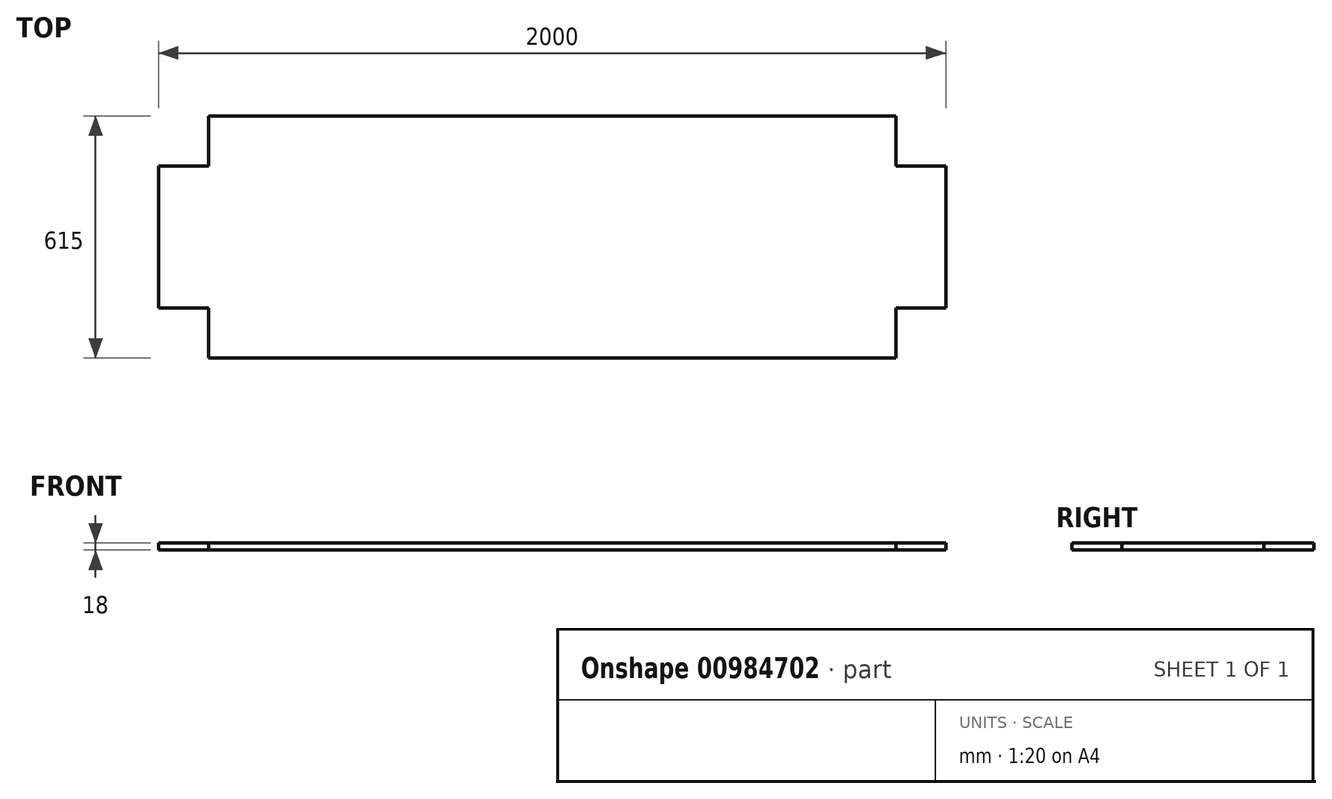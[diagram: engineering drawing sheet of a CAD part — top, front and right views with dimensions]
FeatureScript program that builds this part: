
annotation { "Feature Type Name" : "Feature", "Feature Type Description" : "" }
export const myFeature = defineFeature(function(context is Context, id is Id, definition is map)
    precondition{}
    {
        {
            var Q0;
            Q0=qCreatedBy(makeId("Top.planeOp"),FACE);
            var sketch = newSketch(context, id + "F0", { "sketchPlane" : qUnion([Q0])});
            skLineSegment(sketch, "E0", {"start": v(-259.13, 44.56) * mm, "end": v(-259.13, -316.44) * mm});
            skLineSegment(sketch, "E1", {"start": v(-259.13, -316.44) * mm, "end": v(-132.13, -316.44) * mm});
            skLineSegment(sketch, "E2", {"start": v(-132.13, -316.44) * mm, "end": v(-132.13, -443.44) * mm});
            skLineSegment(sketch, "E3", {"start": v(-132.13, -443.44) * mm, "end": v(1613.87, -443.44) * mm});
            skLineSegment(sketch, "E4", {"start": v(1613.87, -443.44) * mm, "end": v(1613.87, -316.44) * mm});
            skLineSegment(sketch, "E5", {"start": v(1613.87, -316.44) * mm, "end": v(1740.87, -316.44) * mm});
            skLineSegment(sketch, "E6", {"start": v(1740.87, -316.44) * mm, "end": v(1740.87, 44.56) * mm});
            skLineSegment(sketch, "E7", {"start": v(1740.87, 44.56) * mm, "end": v(1613.87, 44.56) * mm});
            skLineSegment(sketch, "E8", {"start": v(1613.87, 44.56) * mm, "end": v(1613.87, 171.56) * mm});
            skLineSegment(sketch, "E9", {"start": v(1613.87, 171.56) * mm, "end": v(-132.13, 171.56) * mm});
            skLineSegment(sketch, "E10", {"start": v(-132.13, 171.56) * mm, "end": v(-132.13, 44.56) * mm});
            skLineSegment(sketch, "E11", {"start": v(-132.13, 44.56) * mm, "end": v(-259.13, 44.56) * mm});
            skSolve(sketch);
        }
        {
            var Q0;
            Q0=makeQuery(id+"F0.imprint","IMPRINT",FACE,{"disambiguationData":[TD([[makeQuery(id+"F0.imprint","IMPRINT",EDGE,{"derivedFrom":sQuery(id+"F0.wireOp",EDGE,"E0")}),1.0]])]});
            extrude(context, id + "F1", {"entities" : qUnion([Q0]), "depth" : 18 * mm, "offsetDistance" : 25 * mm});
        }
    });
